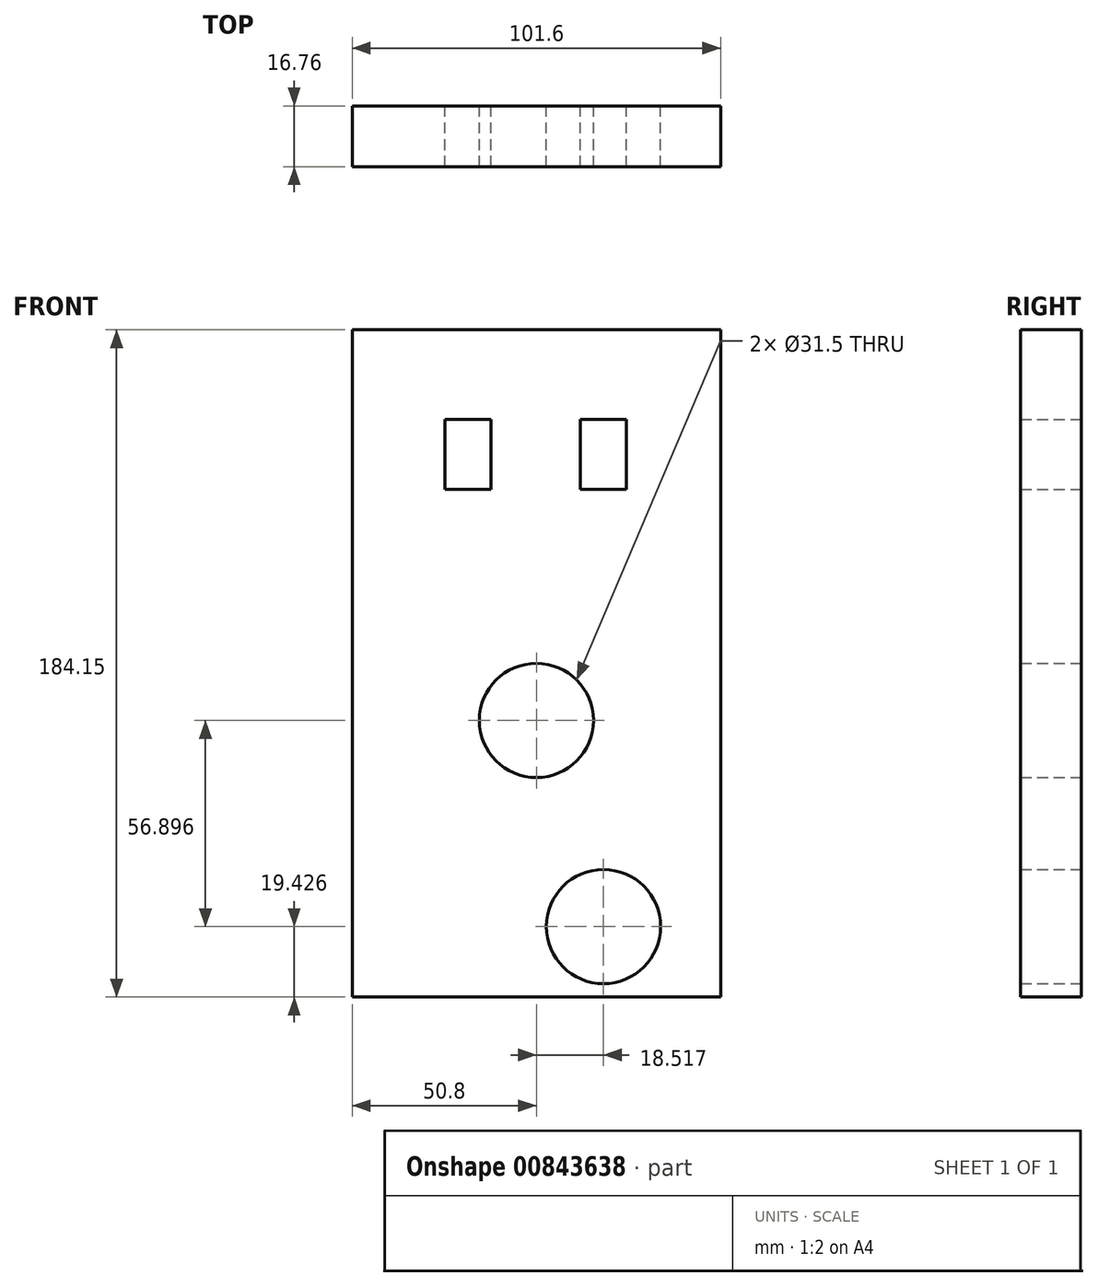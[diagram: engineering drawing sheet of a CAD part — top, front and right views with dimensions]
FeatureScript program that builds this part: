
annotation { "Feature Type Name" : "Feature", "Feature Type Description" : "" }
export const myFeature = defineFeature(function(context is Context, id is Id, definition is map)
    precondition{}
    {
        {
            var Q0;
            Q0=qCreatedBy(makeId("Front.planeOp"),FACE);
            var sketch = newSketch(context, id + "F0", { "sketchPlane" : qUnion([Q0])});
            skCircle(sketch, "E0", {"center": v(18.52, -67.24) * mm, "radius": 15.75 * mm});
            skCircle(sketch, "E1", {"center": v(0, -10.35) * mm, "radius": 15.75 * mm});
            skLineSegment(sketch, "E2.bottom", {"start": v(-25.23, 72.79) * mm, "end": v(-12.53, 72.79) * mm});
            skLineSegment(sketch, "E2.top", {"start": v(-25.23, 53.46) * mm, "end": v(-12.53, 53.46) * mm});
            skLineSegment(sketch, "E2.left", {"start": v(-25.23, 72.79) * mm, "end": v(-25.23, 53.46) * mm});
            skLineSegment(sketch, "E2.right", {"start": v(-12.53, 72.79) * mm, "end": v(-12.53, 53.46) * mm});
            skLineSegment(sketch, "E3.bottom", {"start": v(12.17, 72.79) * mm, "end": v(24.87, 72.79) * mm});
            skLineSegment(sketch, "E3.top", {"start": v(12.17, 53.46) * mm, "end": v(24.87, 53.46) * mm});
            skLineSegment(sketch, "E3.left", {"start": v(12.17, 72.79) * mm, "end": v(12.17, 53.46) * mm});
            skLineSegment(sketch, "E3.right", {"start": v(24.87, 72.79) * mm, "end": v(24.87, 53.46) * mm});
            skPoint(sketch, "E4", {"position": v(18.52, -83) * mm});
            skPoint(sketch, "E5", {"position": v(0, -26.1) * mm});
            skPoint(sketch, "E6", {"position": v(0, 5.4) * mm});
            skPoint(sketch, "E7", {"position": v(18.52, -51.5) * mm});
            skPoint(sketch, "E8", {"position": v(15.75, -10.35) * mm});
            skPoint(sketch, "E9", {"position": v(-15.75, -10.35) * mm});
            skLineSegment(sketch, "E10.bottom", {"start": v(50.8, -86.67) * mm, "end": v(-50.8, -86.67) * mm});
            skLineSegment(sketch, "E10.top", {"start": v(50.8, 97.48) * mm, "end": v(-50.8, 97.48) * mm});
            skLineSegment(sketch, "E10.left", {"start": v(50.8, -86.67) * mm, "end": v(50.8, 97.48) * mm});
            skLineSegment(sketch, "E10.right", {"start": v(-50.8, -86.67) * mm, "end": v(-50.8, 97.48) * mm});
            skSolve(sketch);
        }
        {
            var Q0;
            Q0=makeQuery(id+"F0.imprint","IMPRINT",FACE,{"disambiguationData":[TD([[makeQuery(id+"F0.imprint","IMPRINT",EDGE,{"derivedFrom":sQuery(id+"F0.wireOp",EDGE,"E0")}),-1.0]])]});
            extrude(context, id + "F1", {"entities" : qUnion([Q0]), "depth" : 16.76 * mm, "offsetDistance" : 25.4 * mm});
        }
    });
